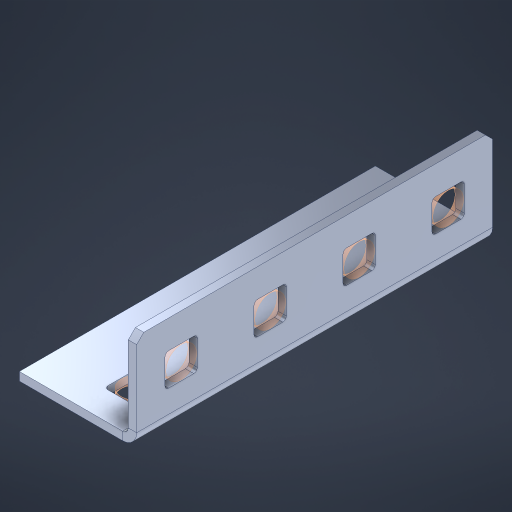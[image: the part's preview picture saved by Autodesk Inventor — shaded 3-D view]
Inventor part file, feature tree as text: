
AUTODESK INVENTOR PART (.ipt)
format: ipt  version: 2023 (Build 270158000, 158)  size: 422,912 bytes
history: native  units: in
note: dims shown in document units (in); Inventor stores cm internally (conversion verified against a paired STEP export)
features: other x13, sheet_metal_op x10, sketch x8, extrude x7, mirror x1, pattern_linear x1, chamfer x1
ambient origin geometry x8: Origin, YZ Plane, XZ Plane, XY Plane, X Axis, Y Axis, Z Axis, Center Point
bodies: Solid1 (feature_tree), Body (feature_tree)
feature tree (41):
  other  "Flange Pattern Plane"
  sheet_metal_op  "Flange Pattern"
  sheet_metal_op  "Body Pattern"
  other  "Arc Length"
  mirror  "Notch Mirror"
  pattern_linear  "Notch Pattern"  Spacing1=0.1875in  [1 undecoded]
  chamfer  "End Chamfer"
  extrude  "Half Cut"  Depth=0.0469in
  sketch  "Sketch1"  dims[d0=2.5in]
  other  "Plate1"
  sketch  "Sketch2"  dims[d1=2.0in]
  other  "Plate2"
  sheet_metal_op  "Bend1"
  sheet_metal_op  "Corner1"
  sketch  "Sketch3"  dims[d2=0.0469in]
  other  "Flange Pattern Sketch"
  sketch  "Sketch7"  dims[d3=0.0469in]
  other  "Srf1"
  other  "Srf2"
  sketch  "Sketch8"  dims[d4=0.0234in]
  sketch  "Sketch9"  dims[d5=0.0938in]
  other  "Srf91"
  sheet_metal_op  "Body Pattern Sketch"
  other  "Srf92"
  sketch  "Sketch13"  dims[d6=0.0469in]
  sketch  "Sketch14"  dims[d7=0.5in d8=90.0deg d9=0.0312in d10=0.1875in d11=0.0469in d12=0.0469in d16=0.182in d17=0.02in d18=0.0469in d19=0.0in d20=0.25in d21=0.25in d46=0.172in d47=1.0in d48=0.0in d49=0.182in d50=0.02in d51=0.25in d52=0.25in d53=0.0469in d54=0.0in d55=0.172in d56=1.0in d57=0.0in d60=1.5748in d62=0.5in d63=0.3937in d65=0.5in d85=0.1227in d86=0.1659in d88=0.04in d89=0.0469in d90=0.0in d91=0.04in d92=0.0491in d95=2.5in d96=0.04in d97=0.25in d98=45.0deg d101=0.0in d102=2.497in d131=0.5in d132=1.5748in d134=0.5in d139=0.5in]
  other  "Srf856"
  other  "Srf1310"
  other  "Srf1311"
  other  "Srf1376"
  sheet_metal_op  "Flange Stamp"
  sheet_metal_op  "Flange Circle"
  sheet_metal_op  "Body Stamp"
  sheet_metal_op  "Body Circle"
  sheet_metal_op  "Notch"
  extrude  "ExtrusionSrf2"  Depth=0.0469in
  extrude  "ExtrusionSrf92"  Depth=0.182in
  extrude  "ExtrusionSrf856"  Depth=0.02in
  extrude  "ExtrusionSrf1310"  Depth=0.0469in
  extrude  "ExtrusionSrf1311"  TaperAngle=0.0deg  [1 undecoded]
  extrude  "ExtrusionSrf1376"  Depth=0.5in
note: 2 required parameter values undecoded (feature->parameter linkage not recoverable at this tier; creation-order binding heuristic only, values carry confidence <= 0.55)
